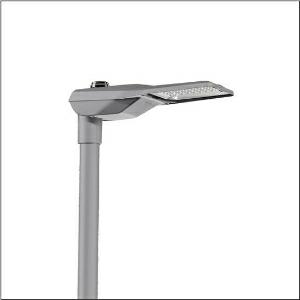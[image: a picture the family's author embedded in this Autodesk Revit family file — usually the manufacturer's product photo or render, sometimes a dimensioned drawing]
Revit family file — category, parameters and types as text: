
# Revit family: streetlight_sl_21_mini___st0_5a_5xe6b47n08gb_d394
name_source: partatom
category: Lighting Fixtures
units: mm (PartAtom-declared; Revit-internal decimal feet)

## family parameters
Cut with Voids When Loaded = No
Host = Face
Light Source = No
Part Type = Normal
Room Calculation Point = No
Round Connector Dimension = Use Diameter
Shared = No

## types (1)
- --- (1 x LED, 6180 lm, 40.4 W, 4000K)
    Apparent Load = 40 VA
    CIE Flux Codes = 41 75 97 100 100
    Color Rendering = 70
    Color Temperature = 4000K
    Default Elevation = 1800 mm
    Description = Streetlight SL 21 mini, mast luminaire, primary light control with lens, of PMMA, primary optical cover: cover, of toughened safety glass, transparent, light distribution: ST0.5a, light emission: direct distribution, primary light characteristic: asymmetric, installation type: side-entry, LED, 3G 1.5mm², High Power LED, rated luminous flux: 6.180lm, luminous efficacy: 153lm/W, light colour: 740, colour temperature: 4000K, control gear: NEMA (7pin), control: overheat protection, pre-setting: linear dimming characteristic, constant luminous flux control, time-dependent luminous flux control, flexible luminous flux parameterisation, mains connection: 230..240V, AC, 50/60Hz, connection cable pre-assembled, cable length: 8,5m, wiring characteristics: H07RN-F, start of lifetime: 40W, end of service life: 41W, reduction: 19W, luminaire housing, of diecast aluminium (EN AC-44300), powder-coated, Siteco® metallic grey (DB 702S), corrosivity category C5 mid according to DIN EN ISO 12944, multi-level sealing system, sealing non-destructively replaceable, inclination adjustable: 0°, 5°, 10°, 15°, length: 628mm, width: 235mm, height: 110mm, spigot size: 42mm (side-entry), mounting height: 4..8m, protection rating (complete): IP66, insulation class (complete): insulation class I (protective earthing), certification: CE, ENEC, ENEC+, VDE, impact resistance: IK10, permissible operating ambient temperature for outdoor applications: -40..+50°C, standard-compliant lighting for roads and squares, packaging unit: 1 piece

Light Distribution: ST0.5a
    Height = 110 mm
    Lamp = 1 x LED
    Lamp Light Flux = 6180 lm
    Lamp Power = 40.4 W
    Lamp count = 1
    Length = 625 mm
    Luminous efficacy = 153 lm/W
    Manufacturer = Siteco
    ModVariant = No
    Model = 5XE6B47N08GB
    Number of Poles = 1
    OnlyDefault = Yes
    Power Factor = 1
    Product Name = Streetlight SL 21 mini | ST0.5a
    Product group = mast luminaire | pylon top
    ProductGroupID = 6100
    Protection Class = Protection class I
    Protection Degree = IP 66
    RLX_Detail_Level = 1
    RLX_Emergency_Light_Flux = 0 lm
    RLX_Emergency_Type = 0
    RLX_Emergency_Type_DB = No
    RlxData = <blob elided: 36821 chars, md5=7213d95e>
    Socket = socket
    Standby Power = 0 W
    System Light Flux = 6180 lm
    System Power = 40 W
    Type Comments = factory setting: luminous flux: 100 % | dim-lin: 254 | 812 mA
    Type Image = l_1294379.jpg
    URL = http://relux.com
    VarID = @adj_137458
    Voltage = 0 V
    Weight = 0.00 kg
    Width = 234 mm

## geometry (parser evidence)
native form markers: Blend x4, Sweep x10
no freeform markers — native parametric forms only
